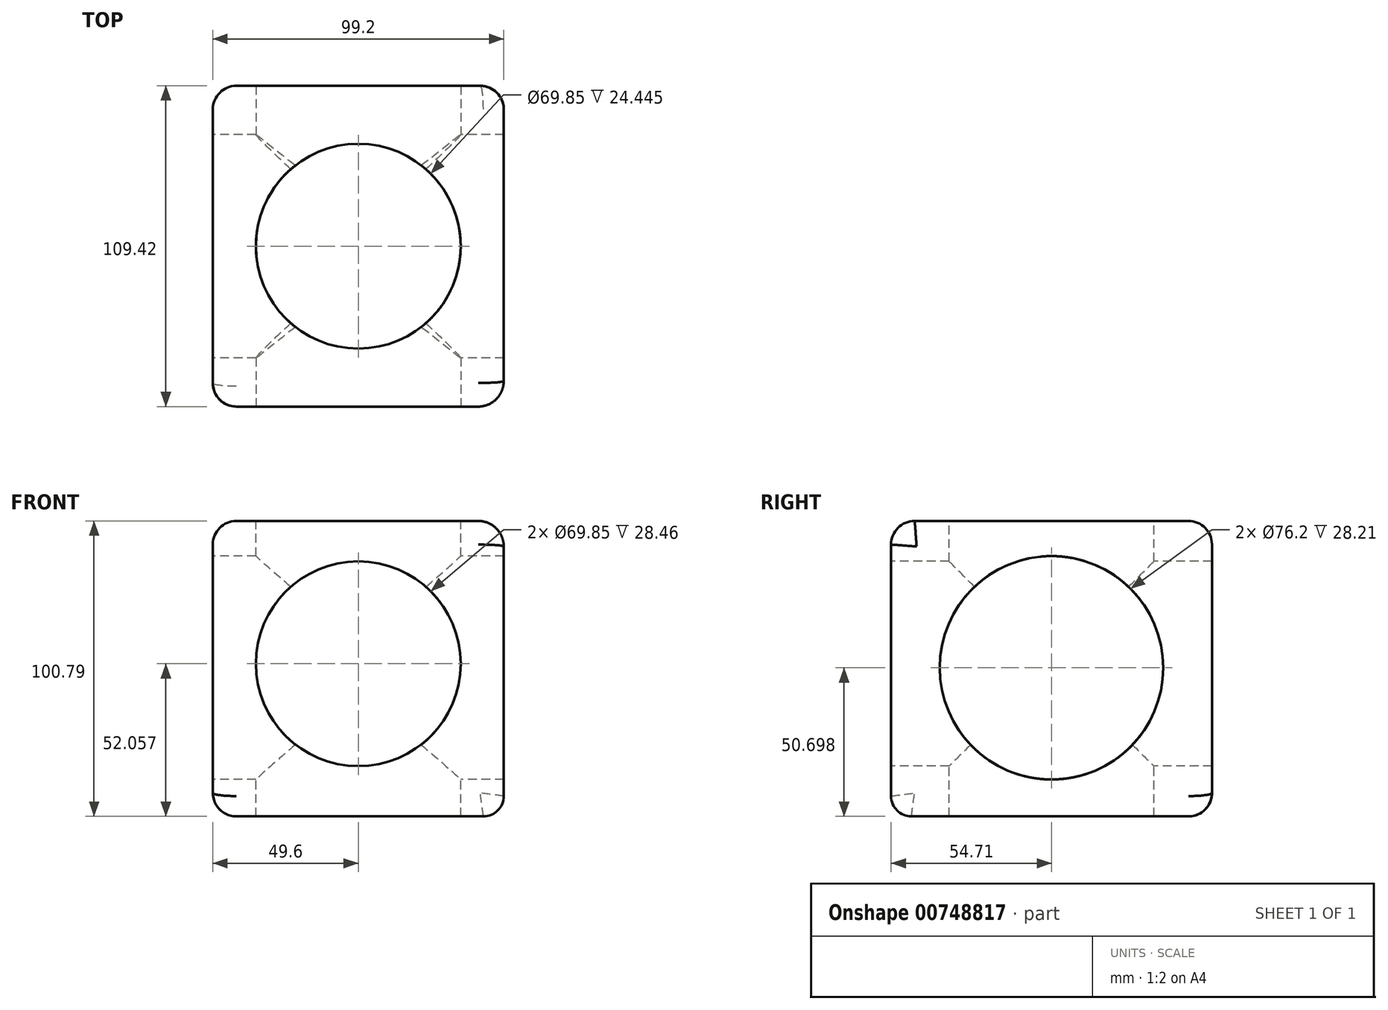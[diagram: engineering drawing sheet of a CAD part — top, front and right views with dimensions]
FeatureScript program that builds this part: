
annotation { "Feature Type Name" : "Feature", "Feature Type Description" : "" }
export const myFeature = defineFeature(function(context is Context, id is Id, definition is map)
    precondition{}
    {
        {
            var Q0;
            Q0=qCreatedBy(makeId("Top.planeOp"),FACE);
            var sketch = newSketch(context, id + "F0", { "sketchPlane" : qUnion([Q0])});
            skLineSegment(sketch, "E0.bottom", {"start": v(49.6, 54.71) * mm, "end": v(-49.6, 54.71) * mm});
            skLineSegment(sketch, "E0.top", {"start": v(49.6, -54.71) * mm, "end": v(-49.6, -54.71) * mm});
            skLineSegment(sketch, "E0.left", {"start": v(49.6, 54.71) * mm, "end": v(49.6, -54.71) * mm});
            skLineSegment(sketch, "E0.right", {"start": v(-49.6, 54.71) * mm, "end": v(-49.6, -54.71) * mm});
            skPoint(sketch, "E0.middle", {"position": v(0, 0) * mm});
            skSolve(sketch);
        }
        {
            var Q0;
            Q0 = qSketchRegion(id + "F0", true);
            extrude(context, id + "F1", {"entities" : qUnion([Q0]), "depth" : 100.8 * mm, "offsetDistance" : 25.4 * mm});
        }
        {
            var Q0;
            Q0=makeQuery(id+"F1.opExtrude","CAP_EDGE",EDGE,{"disambiguationData":[OSD([sQuery(id+"F0.wireOp",EDGE,"E0.top")])],"isStart":false});
            fillet(context, id + "F2", {"entities" : qUnion([Q0]), "radius" : 8.07 * mm, "tangentPropagation" : true, "allowEdgeOverflow" : false});
        }
        {
            var Q0;
            Q0=makeQuery(id+"F1.opExtrude","CAP_EDGE",EDGE,{"disambiguationData":[OSD([sQuery(id+"F0.wireOp",EDGE,"E0.left")])],"isStart":false});
            var Q1;
            {var subQ0=sQuery(id+"F0.wireOp",EDGE,"E0.top");Q1=makeQuery(id+"F2.opFillet","BLEND_EDGE",EDGE,{"blendedFrom":[makeQuery(id+"F1.opExtrude","CAP_EDGE",EDGE,{"disambiguationData":[OSD([subQ0])],"isStart":false}),makeQuery(id+"F1.opExtrude","CAP_FACE",FACE,{"disambiguationData":[OSD([sQuery(id+"F0.wireOp",EDGE,"E0.bottom"),subQ0,sQuery(id+"F0.wireOp",EDGE,"E0.left"),sQuery(id+"F0.wireOp",EDGE,"E0.right")])],"isStart":false})],"blendedInto":[makeQuery(id+"F1.opExtrude","CAP_FACE",FACE,{"disambiguationData":[OSD([sQuery(id+"F0.wireOp",EDGE,"E0.bottom"),subQ0,sQuery(id+"F0.wireOp",EDGE,"E0.left"),sQuery(id+"F0.wireOp",EDGE,"E0.right")])],"isStart":false})]});}
            var Q2;
            {var subQ0=sQuery(id+"F0.wireOp",EDGE,"E0.top");Q2=makeQuery(id+"F2.opFillet","BLEND_EDGE",EDGE,{"blendedFrom":[makeQuery(id+"F1.opExtrude","CAP_EDGE",EDGE,{"disambiguationData":[OSD([subQ0])],"isStart":false}),makeQuery(id+"F1.opExtrude","SWEPT_FACE",FACE,{"disambiguationData":[OSD([subQ0])]})],"blendedInto":[makeQuery(id+"F1.opExtrude","SWEPT_FACE",FACE,{"disambiguationData":[OSD([subQ0])]})]});}
            fillet(context, id + "F3", {"entities" : qUnion([Q0, Q1, Q2]), "radius" : 8.71 * mm, "tangentPropagation" : true, "allowEdgeOverflow" : false});
        }
        {
            var Q0;
            Q0=makeQuery(id+"F1.opExtrude","CAP_EDGE",EDGE,{"disambiguationData":[OSD([sQuery(id+"F0.wireOp",EDGE,"E0.top")])],"isStart":true});
            fillet(context, id + "F4", {"entities" : qUnion([Q0]), "radius" : 6.94 * mm, "tangentPropagation" : true, "allowEdgeOverflow" : false});
        }
        {
            var Q0;
            Q0=makeQuery(id+"F1.opExtrude","CAP_EDGE",EDGE,{"disambiguationData":[OSD([sQuery(id+"F0.wireOp",EDGE,"E0.right")])],"isStart":true});
            var Q1;
            Q1=makeQuery(id+"F1.opExtrude","SWEPT_FACE",FACE,{"disambiguationData":[OSD([sQuery(id+"F0.wireOp",EDGE,"E0.right")])]});
            var Q2;
            Q2=makeQuery(id+"F1.opExtrude","CAP_EDGE",EDGE,{"disambiguationData":[OSD([sQuery(id+"F0.wireOp",EDGE,"E0.bottom")])],"isStart":true});
            fillet(context, id + "F5", {"entities" : qUnion([Q0, Q1, Q2]), "radius" : 8 * mm, "tangentPropagation" : true, "allowEdgeOverflow" : false});
        }
        {
            var Q0;
            Q0=makeQuery(id+"F1.opExtrude","CAP_FACE",FACE,{"disambiguationData":[OSD([sQuery(id+"F0.wireOp",EDGE,"E0.bottom"),sQuery(id+"F0.wireOp",EDGE,"E0.top"),sQuery(id+"F0.wireOp",EDGE,"E0.left"),sQuery(id+"F0.wireOp",EDGE,"E0.right")])],"isStart":false});
            var sketch = newSketch(context, id + "F6", { "sketchPlane" : qUnion([Q0])});
            skCircle(sketch, "E1", {"center": v(0, 0) * mm, "radius": 34.72 * mm});
            skSolve(sketch);
        }
        {
            var Q0;
            Q0=sQuery(id+"F6.wireOp",VERTEX,"E1.center");
            var Q1;
            Q1=makeQuery(id+"F1.opExtrude","SWEPT_BODY",BODY,{"disambiguationData":[OSD([sQuery(id+"F0.wireOp",EDGE,"E0.bottom"),sQuery(id+"F0.wireOp",EDGE,"E0.top"),sQuery(id+"F0.wireOp",EDGE,"E0.left"),sQuery(id+"F0.wireOp",EDGE,"E0.right")])]});
            hole(context, id + "F7", {"style" : HoleStyle.SIMPLE, "endStyle" : HoleEndStyle.THROUGH, "holeDiameter" : 69.85 * mm, "majorDiameter" : 6.35 * mm, "isTappedThrough" : true, "tappedDepth" : 12.7 * mm, "tapClearance" : 3, "locations" : qUnion([Q0]), "scope" : qUnion([Q1])});
        }
        {
            var Q0;
            Q0=makeQuery(id+"F1.opExtrude","SWEPT_FACE",FACE,{"disambiguationData":[OSD([sQuery(id+"F0.wireOp",EDGE,"E0.top")])]});
            var sketch = newSketch(context, id + "F8", { "sketchPlane" : qUnion([Q0])});
            skCircle(sketch, "E2", {"center": v(0, 52.06) * mm, "radius": 34.94 * mm});
            skSolve(sketch);
        }
        {
            var Q0;
            Q0=sQuery(id+"F8.wireOp",VERTEX,"E2.center");
            var Q1;
            Q1=makeQuery(id+"F1.opExtrude","SWEPT_BODY",BODY,{"disambiguationData":[OSD([sQuery(id+"F0.wireOp",EDGE,"E0.bottom"),sQuery(id+"F0.wireOp",EDGE,"E0.top"),sQuery(id+"F0.wireOp",EDGE,"E0.left"),sQuery(id+"F0.wireOp",EDGE,"E0.right")])]});
            hole(context, id + "F9", {"style" : HoleStyle.SIMPLE, "endStyle" : HoleEndStyle.THROUGH, "holeDiameter" : 69.85 * mm, "majorDiameter" : 6.35 * mm, "isTappedThrough" : true, "tappedDepth" : 12.7 * mm, "tapClearance" : 3, "locations" : qUnion([Q0]), "scope" : qUnion([Q1])});
        }
        {
            var Q0;
            Q0=makeQuery(id+"F1.opExtrude","SWEPT_FACE",FACE,{"disambiguationData":[OSD([sQuery(id+"F0.wireOp",EDGE,"E0.right")])]});
            var sketch = newSketch(context, id + "F10", { "sketchPlane" : qUnion([Q0])});
            skCircle(sketch, "E3", {"center": v(0, 50.7) * mm, "radius": 37.4 * mm});
            skSolve(sketch);
        }
        {
            var Q0;
            Q0=sQuery(id+"F10.wireOp",VERTEX,"E3.center");
            var Q1;
            Q1=makeQuery(id+"F1.opExtrude","SWEPT_BODY",BODY,{"disambiguationData":[OSD([sQuery(id+"F0.wireOp",EDGE,"E0.bottom"),sQuery(id+"F0.wireOp",EDGE,"E0.top"),sQuery(id+"F0.wireOp",EDGE,"E0.left"),sQuery(id+"F0.wireOp",EDGE,"E0.right")])]});
            hole(context, id + "F11", {"style" : HoleStyle.SIMPLE, "endStyle" : HoleEndStyle.THROUGH, "holeDiameter" : 76.2 * mm, "majorDiameter" : 6.35 * mm, "isTappedThrough" : true, "tappedDepth" : 12.7 * mm, "tapClearance" : 3, "locations" : qUnion([Q0]), "scope" : qUnion([Q1])});
        }
    });
